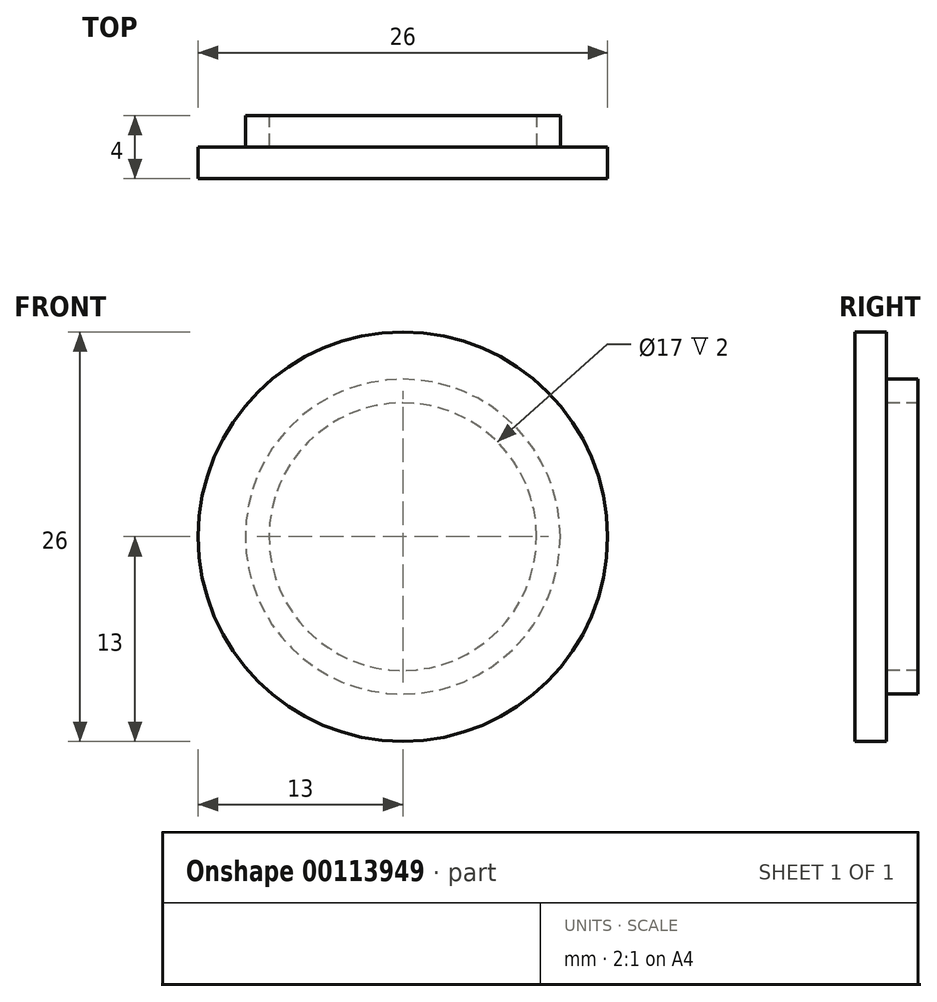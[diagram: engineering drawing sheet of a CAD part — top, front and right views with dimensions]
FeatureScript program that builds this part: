
annotation { "Feature Type Name" : "Feature", "Feature Type Description" : "" }
export const myFeature = defineFeature(function(context is Context, id is Id, definition is map)
    precondition{}
    {
        {
            var Q0;
            Q0=qCreatedBy(makeId("Front.planeOp"),FACE);
            var sketch = newSketch(context, id + "F0", { "sketchPlane" : qUnion([Q0])});
            skCircle(sketch, "E0", {"center": v(0, 0) * mm, "radius": 10 * mm});
            skCircle(sketch, "E1.0", {"center": v(0, 0) * mm, "radius": 13 * mm});
            skCircle(sketch, "E2.0", {"center": v(0, 0) * mm, "radius": 8.5 * mm});
            skSolve(sketch);
        }
        {
            var Q0;
            Q0=makeQuery(id+"F0.imprint","IMPRINT",FACE,{"disambiguationData":[TD([[makeQuery(id+"F0.imprint","IMPRINT",EDGE,{"derivedFrom":sQuery(id+"F0.wireOp",EDGE,"E0")}),-1.0]])]});
            extrude(context, id + "F1", {"entities" : qUnion([Q0]), "oppositeDirection" : true, "depth" : 2 * mm});
        }
        {
            var Q0;
            Q0=makeQuery(id+"F0.imprint","IMPRINT",FACE,{"disambiguationData":[TD([[makeQuery(id+"F0.imprint","IMPRINT",EDGE,{"derivedFrom":sQuery(id+"F0.wireOp",EDGE,"E0")}),1.0]])]});
            extrude(context, id + "F2", {"entities" : qUnion([Q0]), "operationType" : NewBodyOperationType.ADD, "oppositeDirection" : true, "depth" : 4 * mm});
        }
        {
            var Q0;
            Q0=makeQuery(id+"F0.imprint","IMPRINT",FACE,{"disambiguationData":[TD([[makeQuery(id+"F0.imprint","IMPRINT",EDGE,{"derivedFrom":sQuery(id+"F0.wireOp",EDGE,"E2.0")}),1.0]])]});
            extrude(context, id + "F3", {"entities" : qUnion([Q0]), "operationType" : NewBodyOperationType.ADD, "oppositeDirection" : true, "depth" : 2 * mm});
        }
    });
